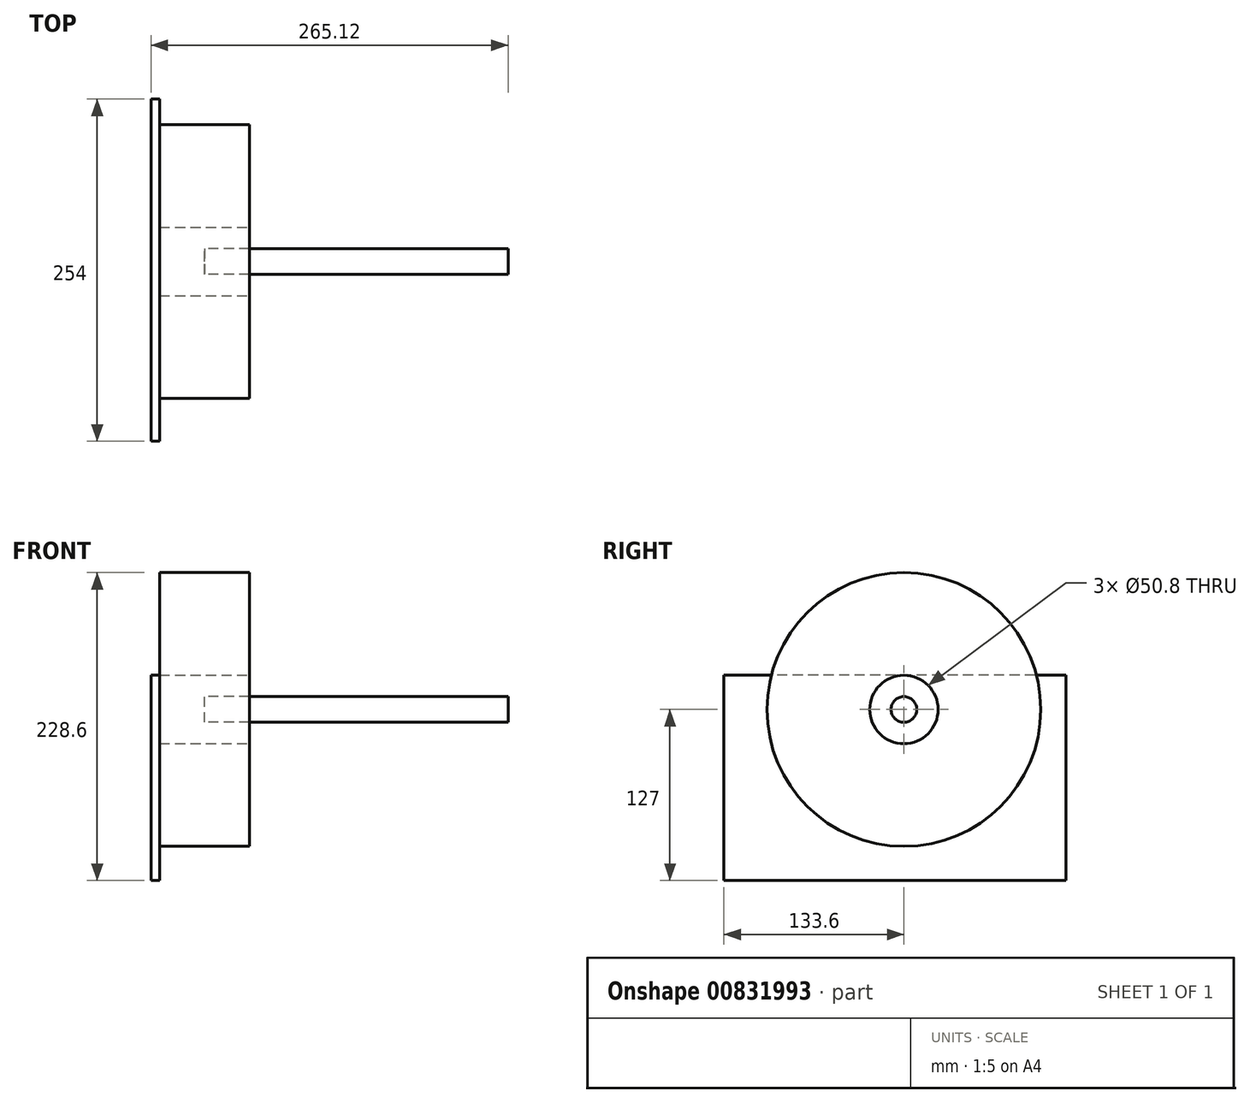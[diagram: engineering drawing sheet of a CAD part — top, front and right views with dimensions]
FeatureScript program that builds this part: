
annotation { "Feature Type Name" : "Feature", "Feature Type Description" : "" }
export const myFeature = defineFeature(function(context is Context, id is Id, definition is map)
    precondition{}
    {
        {
            var Q0;
            Q0=qCreatedBy(makeId("Right.planeOp"),FACE);
            var sketch = newSketch(context, id + "F0", { "sketchPlane" : qUnion([Q0])});
            skCircle(sketch, "E0", {"center": v(0, 0) * mm, "radius": 101.6 * mm});
            skSolve(sketch);
        }
        {
            var Q0;
            Q0 = qSketchRegion(id + "F0", true);
            extrude(context, id + "F1", {"entities" : qUnion([Q0]), "endBound" : BoundingType.SYMMETRIC, "depth" : 66.67 * mm, "offsetDistance" : 25.4 * mm});
        }
        {
            var Q0;
            Q0=makeQuery(id+"F1.opExtrude","CAP_FACE",FACE,{"disambiguationData":[OSD([sQuery(id+"F0.wireOp",EDGE,"E0")])],"isStart":false});
            var sketch = newSketch(context, id + "F2", { "sketchPlane" : qUnion([Q0])});
            skCircle(sketch, "E1", {"center": v(0, 0) * mm, "radius": 25.4 * mm});
            skPoint(sketch, "E2", {"position": v(0, 25.4) * mm});
            skSolve(sketch);
        }
        {
            var Q0;
            Q0=makeQuery(id+"F2.imprint","IMPRINT",FACE,{"disambiguationData":[TD([[makeQuery(id+"F2.imprint","IMPRINT",EDGE,{"derivedFrom":sQuery(id+"F2.wireOp",EDGE,"E1")}),1.0]])]});
            var Q1;
            Q1=sQuery(id+"F2.wireOp",EDGE,"E1");
            extrude(context, id + "F3", {"entities" : qUnion([Q0]), "operationType" : NewBodyOperationType.REMOVE, "surfaceEntities" : qUnion([Q1]), "endBound" : BoundingType.THROUGH_ALL, "oppositeDirection" : true, "depth" : 25.4 * mm, "offsetDistance" : 25.4 * mm});
        }
        {
            var Q0;
            Q0=makeQuery(id+"F1.opExtrude","SWEPT_BODY",BODY,{"disambiguationData":[OSD([sQuery(id+"F0.wireOp",EDGE,"E0")])]});
            transform(context, id + "F4", {"entities" : qUnion([Q0]), "transformType" : TransformType.TRANSLATION_3D, "dx" : 0 * mm, "dy" : 0 * mm, "dz" : 0 * mm, "makeCopy" : true});
        }
        {
            var Q0;
            Q0=makeQuery(id+"F4.opPattern","COPY",BODY,{"derivedFrom":makeQuery(id+"F1.opExtrude","SWEPT_BODY",BODY,{"disambiguationData":[OSD([sQuery(id+"F0.wireOp",EDGE,"E0")])]}),"instanceName":"1"});
            transform(context, id + "F5", {"entities" : qUnion([Q0]), "transformType" : TransformType.TRANSLATION_3D, "dx" : 0 * mm, "dy" : 0 * mm, "dz" : 0 * mm, "makeCopy" : true});
        }
        {
            var Q0;
            Q0=makeQuery(id+"F0.imprint","IMPRINT",FACE,{"disambiguationData":[TD([[makeQuery(id+"F0.imprint","IMPRINT",EDGE,{"derivedFrom":sQuery(id+"F0.wireOp",EDGE,"E0")}),1.0]])]});
            var sketch = newSketch(context, id + "F6", { "sketchPlane" : qUnion([Q0])});
            skCircle(sketch, "E3", {"center": v(0, 0) * mm, "radius": 9.53 * mm});
            skPoint(sketch, "E4", {"position": v(0, 9.53) * mm});
            skSolve(sketch);
        }
        {
            var Q0;
            Q0 = qSketchRegion(id + "F6", true);
            extrude(context, id + "F7", {"entities" : qUnion([Q0]), "depth" : 225.42 * mm, "offsetDistance" : 25.4 * mm});
        }
        {
            var Q0;
            Q0=makeQuery(id+"F1.opExtrude","CAP_FACE",FACE,{"disambiguationData":[OSD([sQuery(id+"F0.wireOp",EDGE,"E0")])],"isStart":true});
            var sketch = newSketch(context, id + "F8", { "sketchPlane" : qUnion([Q0])});
            skLineSegment(sketch, "E5.bottom", {"start": v(-120.4, 25.4) * mm, "end": v(133.6, 25.4) * mm});
            skLineSegment(sketch, "E5.top", {"start": v(-120.4, -127) * mm, "end": v(133.6, -127) * mm});
            skLineSegment(sketch, "E5.left", {"start": v(-120.4, 25.4) * mm, "end": v(-120.4, -127) * mm});
            skLineSegment(sketch, "E5.right", {"start": v(133.6, 25.4) * mm, "end": v(133.6, -127) * mm});
            skSolve(sketch);
        }
        {
            var Q0;
            Q0 = qSketchRegion(id + "F8", true);
            extrude(context, id + "F9", {"entities" : qUnion([Q0]), "depth" : 6.35 * mm, "offsetDistance" : 25.4 * mm});
        }
    });
